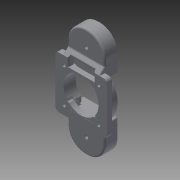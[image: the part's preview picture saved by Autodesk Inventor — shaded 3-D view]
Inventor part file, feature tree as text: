
AUTODESK INVENTOR PART (.ipt)
format: ipt  version: 2014 (Build 180170000, 170)  size: 508,928 bytes
history: native  units: in
note: dims shown in document units (in); Inventor stores cm internally (conversion verified against a paired STEP export)
features: extrude x10, sketch x10, reference x9, fillet x6, projected_geometry x2, plane x1, chamfer x1
ambient origin geometry x8: Origin, YZ Plane, XZ Plane, XY Plane, X Axis, Y Axis, Z Axis, Center Point
bodies: Solid1 (feature_tree)
feature tree (39):
  plane  "Work Plane1"
  extrude  "Extrusion1"  Depth=3.73in
  extrude  "Extrusion3"  Depth=0.864in
  extrude  "Extrusion5"  Depth=0.239in
  extrude  "Extrusion6"  Depth=0.1732in TaperAngle=0.0deg
  extrude  "Extrusion7"  Depth=0.125in
  extrude  "Extrusion8"  Depth=0.18in
  extrude  "Extrusion10"  Depth=0.25in
  extrude  "Extrusion11"  Depth=0.125in
  fillet  "Fillet1"  Radius=0.25in
  extrude  "Extrusion12"  Depth=0.125in
  chamfer  "Chamfer1"  Distance=0.3in
  fillet  "Fillet2"  Radius=0.18in
  fillet  "Fillet3"  Radius=0.1339in
  fillet  "Fillet4"  Radius=0.1339in
  fillet  "Fillet5"  Radius=0.0118in
  extrude  "Extrusion13"  TaperAngle=0.0deg  [1 undecoded]
  fillet  "Fillet6"  Radius=0.125in
  sketch  "Sketch1"  dims[d0=1.27in d1=3.73in]
  reference  "Reference1"
  sketch  "Sketch2"  dims[d2=0.2in d3=0.0in d4=0.864in]
  reference  "Reference2"
  reference  "Reference3"
  reference  "Reference4"
  reference  "Reference5"
  reference  "Reference6"
  reference  "Reference7"
  reference  "Reference8"
  reference  "Reference9"
  projected_geometry  "Projected Loop1"
  sketch  "Sketch4"  dims[d7=0.239in d8=0.0in d9=1.7717in]
  sketch  "Sketch5"  dims[d10=1.7717in d19=0.1732in d20=0.0in]
  sketch  "Sketch6"  dims[d21=0.1732in d22=0.0in d23=0.125in]
  sketch  "Sketch7"  dims[d25=0.125in d26=0.18in]
  sketch  "Sketch8"  dims[d27=0.125in d28=0.25in]
  projected_geometry  "Projected Loop2"
  sketch  "Sketch9"  dims[d29=0.3in d30=0.0in d31=0.125in d32=0.25in]
  sketch  "Sketch10"  dims[d33=0.125in d34=0.125in d35=0.3in d36=0.0in d37=0.18in d38=0.1339in d39=0.1339in d42=0.0118in d43=0.0in]
  sketch  "Sketch11"  dims[d44=1.2in d45=0.0in d46=0.0in d47=0.125in d48=0.173in d49=0.173in d50=0.0in d51=0.173in d52=0.125in d53=45.0deg d54=0.05in d55=0.6in d56=0.06in d57=0.06in d58=0.15in d59=1.0in d60=0.0in d61=0.0394in d62=1.2205in d63=1.2205in d64=0.1181in d65=0.1181in d66=0.1181in d67=0.1181in]
note: 1 required parameter value undecoded (feature->parameter linkage not recoverable at this tier; creation-order binding heuristic only, values carry confidence <= 0.55)
